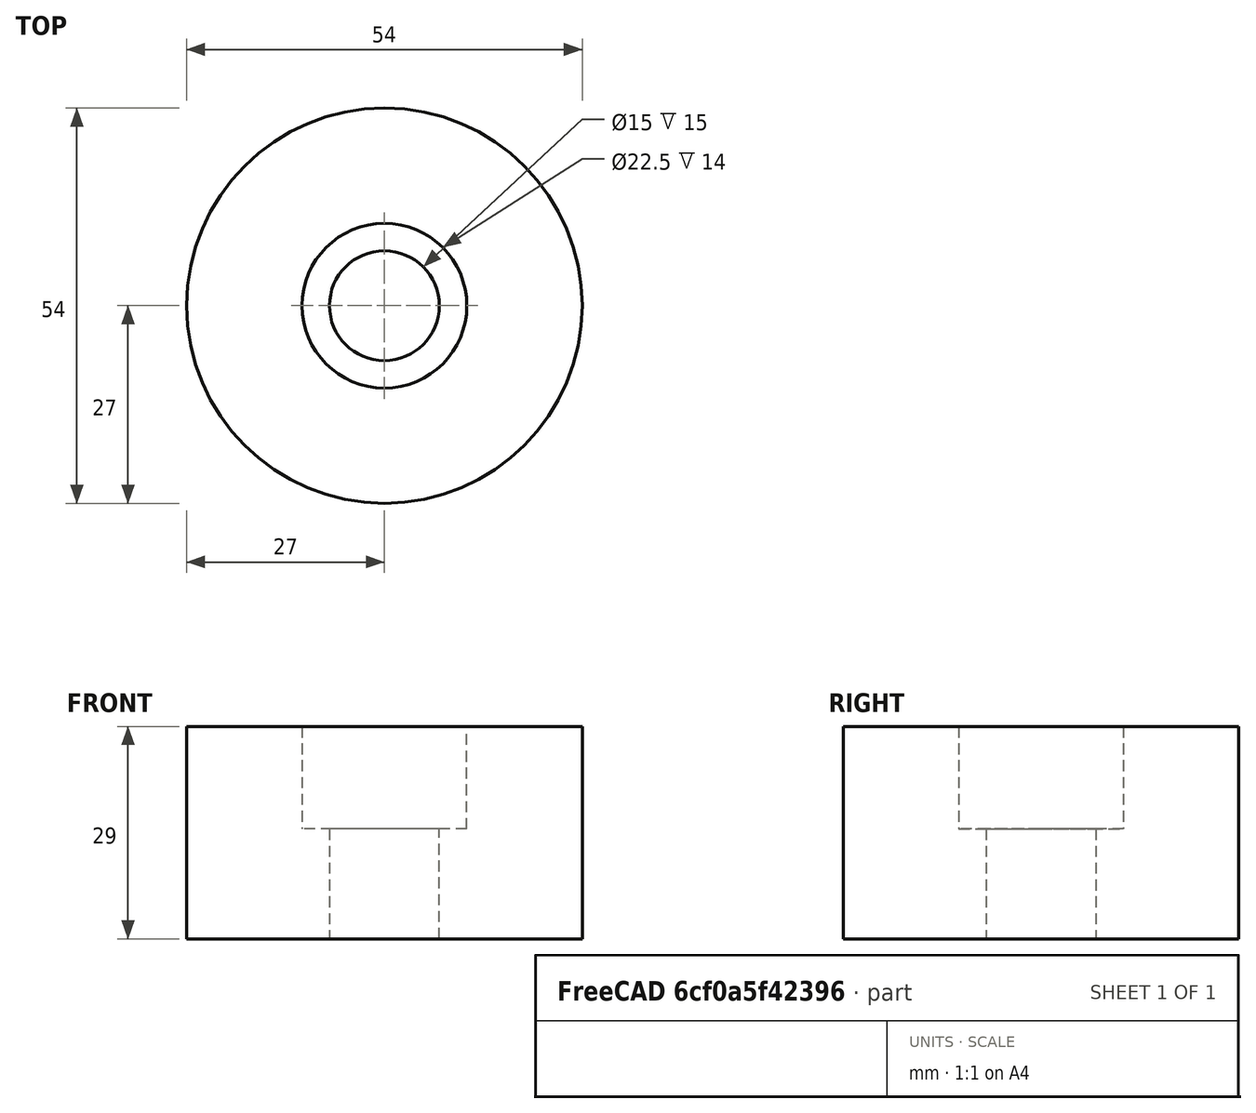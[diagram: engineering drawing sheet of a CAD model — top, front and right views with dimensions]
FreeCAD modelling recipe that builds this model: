
FCSTD DOCUMENT  (FreeCAD 1.0R1.0rc2)
Label: SpoolAdapter_54mm
License: All rights reserved
LicenseURL: http://en.wikipedia.org/wiki/All_rights_reserved
objects: Part::Cylinder×3, Spreadsheet::Sheet×1, Part::MultiFuse×1, Part::Cut×1
note: 5 computed .brp shape members not serialized (recipe doc carries the construction recipe); baked Part::Feature solids carry a one-line shape summary decoded from their .brp

FEATURE [Spreadsheet::Sheet] Spreadsheet  label="SpoolAdapter"
  cells = A1='Spool properties; A2='Spool diameter; B2(spool_dia_od)=300; A3='Spool inner diameter; B3(spool_id_dia)=55; A4='Inner diameter tolerance; B4(spool_id_tolerance)=1; A5='Effective inner spool diameter; B5(spool_effective_id)==B3 - B4; A6='Spool thickness; B6(spool_thickness)=100; A7='Axis and bearing; A8='Axle diameter; B8(axis_dia)=8.4; A9='Bearing OD; B9(bearing_od)=22.5; A10='Bearing Thickness; B10(bearing_thickness)==7 + 7; A11='Axle hole diameter; B11(axis_hole)=15; A12='Base model; A13='Wall thickness; B13(wall_thickness)=15
FEATURE [Part::Cylinder] Cylinder
  Angle = 360
  AttacherType = Attacher::AttachEngine3D
  FirstAngle = 0
  Height = 29
  Radius = 27
  SecondAngle = 0
  expr: Height = <<SpoolAdapter>>.bearing_thickness + <<SpoolAdapter>>.wall_thickness
  expr: Radius = <<SpoolAdapter>>.spool_effective_id / 2
FEATURE [Part::Cylinder] Cylinder001
  Angle = 360
  AttacherType = Attacher::AttachEngine3D
  FirstAngle = 0
  Height = 29
  Radius = 7.5
  SecondAngle = 0
  expr: Height = <<SpoolAdapter>>.bearing_thickness + <<SpoolAdapter>>.wall_thickness
  expr: Radius = <<SpoolAdapter>>.axis_hole / 2
FEATURE [Part::Cylinder] Cylinder002
  Angle = 360
  AttacherType = Attacher::AttachEngine3D
  FirstAngle = 0
  Height = 14
  Placement = pos=(0,0,15) rot=(0,0,1;0rad)
  Radius = 11.25
  SecondAngle = 0
  expr: .Placement.Base.z = <<SpoolAdapter>>.wall_thickness
  expr: Height = <<SpoolAdapter>>.bearing_thickness
  expr: Radius = <<SpoolAdapter>>.bearing_od / 2
FEATURE [Part::MultiFuse] Fusion
  Shapes = -> [Cylinder001,Cylinder002]
FEATURE [Part::Cut] Cut  label="SingleAdapter"
  Base = -> Cylinder
  Tool = -> Fusion
